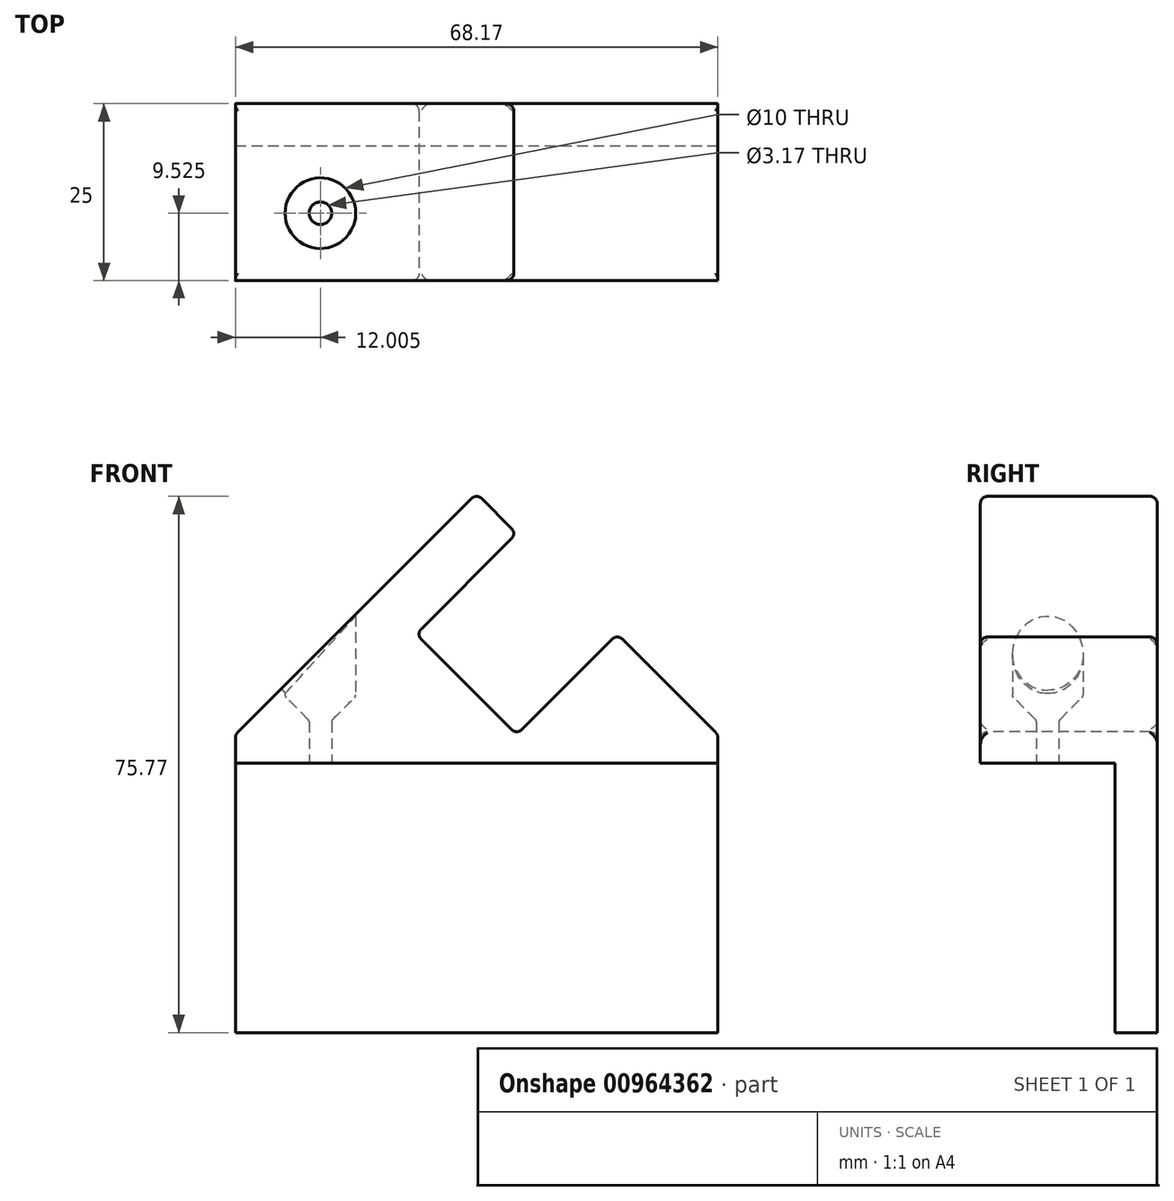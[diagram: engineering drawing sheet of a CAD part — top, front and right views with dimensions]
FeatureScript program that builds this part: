
annotation { "Feature Type Name" : "Feature", "Feature Type Description" : "" }
export const myFeature = defineFeature(function(context is Context, id is Id, definition is map)
    precondition{}
    {
        {
            var Q0;
            Q0=qCreatedBy(makeId("Front.planeOp"),FACE);
            var sketch = newSketch(context, id + "F0", { "sketchPlane" : qUnion([Q0])});
            skLineSegment(sketch, "E0", {"start": v(-68.17, 42.1) * mm, "end": v(-68.17, 0) * mm});
            skLineSegment(sketch, "E1", {"start": v(-68.17, 0) * mm, "end": v(0, 0) * mm});
            skLineSegment(sketch, "E2", {"start": v(0, 0) * mm, "end": v(0, 42.1) * mm});
            skLineSegment(sketch, "E3", {"start": v(0, 42.1) * mm, "end": v(-14.21, 56.31) * mm});
            skLineSegment(sketch, "E4", {"start": v(-14.21, 56.31) * mm, "end": v(-28.43, 42.1) * mm});
            skLineSegment(sketch, "E5", {"start": v(-28.43, 42.1) * mm, "end": v(-42.64, 56.31) * mm});
            skLineSegment(sketch, "E6", {"start": v(-42.64, 56.31) * mm, "end": v(-28.43, 70.53) * mm});
            skLineSegment(sketch, "E7", {"start": v(-28.43, 70.53) * mm, "end": v(-34.08, 76.18) * mm});
            skLineSegment(sketch, "E8", {"start": v(-34.08, 76.18) * mm, "end": v(-68.17, 42.1) * mm});
            skLineSegment(sketch, "E9", {"start": v(0, 42.1) * mm, "end": v(-68.17, 42.1) * mm, "construction": true});
            skLineSegment(sketch, "E10", {"start": v(-68.17, 38.1) * mm, "end": v(0, 38.1) * mm, "construction": true});
            skLineSegment(sketch, "E11", {"start": v(-28.43, 70.53) * mm, "end": v(-14.21, 56.31) * mm, "construction": true});
            skSolve(sketch);
        }
        {
            var Q0;
            Q0=makeQuery(id+"F0.imprint","IMPRINT",FACE,{"disambiguationData":[TD([[makeQuery(id+"F0.imprint","IMPRINT",EDGE,{"derivedFrom":sQuery(id+"F0.wireOp",EDGE,"E0")}),1.0]])]});
            extrude(context, id + "F1", {"entities" : qUnion([Q0]), "depth" : 25 * mm, "offsetDistance" : 25 * mm});
        }
        {
            var Q0;
            Q0=makeQuery(id+"F1.opExtrude","SWEPT_FACE",FACE,{"disambiguationData":[OSD([sQuery(id+"F0.wireOp",EDGE,"E2")])]});
            var sketch = newSketch(context, id + "F2", { "sketchPlane" : qUnion([Q0])});
            skLineSegment(sketch, "E12.0.0", {"start": v(0, 0) * mm, "end": v(0, 42.1) * mm, "construction": true});
            skLineSegment(sketch, "E12.0.1", {"start": v(0, 42.1) * mm, "end": v(-25, 42.1) * mm, "construction": true});
            skLineSegment(sketch, "E12.0.2", {"start": v(-25, 42.1) * mm, "end": v(-25, 0) * mm, "construction": true});
            skLineSegment(sketch, "E12.0.3", {"start": v(-25, 0) * mm, "end": v(0, 0) * mm, "construction": true});
            skLineSegment(sketch, "E13.bottom", {"start": v(-25, 38.1) * mm, "end": v(-5.95, 38.1) * mm});
            skLineSegment(sketch, "E13.top", {"start": v(-25, 0) * mm, "end": v(-5.95, 0) * mm});
            skLineSegment(sketch, "E13.left", {"start": v(-25, 38.1) * mm, "end": v(-25, 0) * mm});
            skLineSegment(sketch, "E13.right", {"start": v(-5.95, 38.1) * mm, "end": v(-5.95, 0) * mm});
            skSolve(sketch);
        }
        {
            var Q0;
            Q0=makeQuery(id+"F2.imprint","IMPRINT",FACE,{"disambiguationData":[TD([[makeQuery(id+"F2.imprint","IMPRINT",EDGE,{"derivedFrom":sQuery(id+"F2.wireOp",EDGE,"E13.bottom")}),-1.0]])]});
            extrude(context, id + "F3", {"entities" : qUnion([Q0]), "operationType" : NewBodyOperationType.REMOVE, "endBound" : BoundingType.THROUGH_ALL, "oppositeDirection" : true, "depth" : 25 * mm, "offsetDistance" : 25 * mm});
        }
        {
            var Q0;
            Q0=makeQuery(id+"F1.opExtrude","SWEPT_FACE",FACE,{"disambiguationData":[OSD([sQuery(id+"F0.wireOp",EDGE,"E6")])]});
            var Q1;
            Q1=makeQuery(id+"F1.opExtrude","SWEPT_FACE",FACE,{"disambiguationData":[OSD([sQuery(id+"F0.wireOp",EDGE,"E4")])]});
            var Q2;
            Q2=makeQuery(id+"F1.opExtrude","SWEPT_FACE",FACE,{"disambiguationData":[OSD([sQuery(id+"F0.wireOp",EDGE,"E8")])]});
            var Q3;
            Q3=makeQuery(id+"F1.opExtrude","SWEPT_FACE",FACE,{"disambiguationData":[OSD([sQuery(id+"F0.wireOp",EDGE,"E3")])]});
            var Q4;
            Q4=makeQuery(id+"F1.opExtrude","SWEPT_FACE",FACE,{"disambiguationData":[OSD([sQuery(id+"F0.wireOp",EDGE,"E7")])]});
            fillet(context, id + "F4", {"entities" : qUnion([Q0, Q1, Q2, Q3, Q4]), "radius" : 1 * mm, "tangentPropagation" : true, "allowEdgeOverflow" : false});
        }
        {
            var Q0;
            Q0=makeQuery(id+"F3.boolean.opBoolean","COPY",FACE,{"derivedFrom":makeQuery(id+"F3.opExtrude","SWEPT_FACE",FACE,{"disambiguationData":[OSD([sQuery(id+"F2.wireOp",EDGE,"E13.bottom")])]})});
            var sketch = newSketch(context, id + "F5", { "sketchPlane" : qUnion([Q0])});
            skLineSegment(sketch, "E14.0.0", {"start": v(-68.17, 25) * mm, "end": v(-68.17, 5.95) * mm, "construction": true});
            skLineSegment(sketch, "E14.0.1", {"start": v(-68.17, 5.95) * mm, "end": v(0, 5.95) * mm, "construction": true});
            skLineSegment(sketch, "E14.0.2", {"start": v(0, 5.95) * mm, "end": v(0, 25) * mm, "construction": true});
            skLineSegment(sketch, "E14.0.3", {"start": v(0, 25) * mm, "end": v(-68.17, 25) * mm, "construction": true});
            skLineSegment(sketch, "E15", {"start": v(-68.17, 15.48) * mm, "end": v(0, 15.48) * mm, "construction": true});
            skLineSegment(sketch, "E16", {"start": v(-56.17, 25) * mm, "end": v(-56.17, 5.95) * mm, "construction": true});
            skCircle(sketch, "E17", {"center": v(-56.17, 15.48) * mm, "radius": 1.59 * mm});
            skCircle(sketch, "E18", {"center": v(-56.17, 15.48) * mm, "radius": 5 * mm});
            skSolve(sketch);
        }
        {
            var Q0;
            Q0=makeQuery(id+"F5.imprint","IMPRINT",FACE,{"disambiguationData":[TD([[makeQuery(id+"F5.imprint","IMPRINT",EDGE,{"derivedFrom":sQuery(id+"F5.wireOp",EDGE,"E17")}),1.0]])]});
            var Q1;
            Q1=makeQuery(id+"F5.imprint","IMPRINT",FACE,{"disambiguationData":[TD([[makeQuery(id+"F5.imprint","IMPRINT",EDGE,{"derivedFrom":sQuery(id+"F5.wireOp",EDGE,"E17")}),-1.0]])]});
            extrude(context, id + "F6", {"entities" : qUnion([Q0, Q1]), "operationType" : NewBodyOperationType.REMOVE, "endBound" : BoundingType.THROUGH_ALL, "oppositeDirection" : true, "depth" : 25 * mm, "offsetDistance" : 25 * mm});
        }
        {
            var Q0;
            Q0=makeQuery(id+"F5.imprint","IMPRINT",FACE,{"disambiguationData":[TD([[makeQuery(id+"F5.imprint","IMPRINT",EDGE,{"derivedFrom":sQuery(id+"F5.wireOp",EDGE,"E17")}),-1.0]])]});
            extrude(context, id + "F7", {"entities" : qUnion([Q0]), "operationType" : NewBodyOperationType.ADD, "oppositeDirection" : true, "depth" : 10 * mm, "offsetDistance" : 25 * mm});
        }
        {
            var Q0;
            Q0=makeQuery(id+"F7.opExtrude","CAP_EDGE",EDGE,{"disambiguationData":[OSD([sQuery(id+"F5.wireOp",EDGE,"E17")])],"isStart":false});
            chamfer(context, id + "F8", {"entities" : qUnion([Q0]), "width" : 4 * mm, "tangentPropagation" : true});
        }
        {
            var Q0;
            Q0=makeQuery(id+"F6.boolean.opBoolean","COPY",FACE,{"derivedFrom":makeQuery(id+"F6.opExtrude","SWEPT_FACE",FACE,{"disambiguationData":[OSD([sQuery(id+"F5.wireOp",EDGE,"E18")])]})});
            var Q1;
            {var subQ0=sQuery(id+"F5.wireOp",EDGE,"E17");Q1=makeQuery(id+"F8.opChamfer","BLEND_EDGE",EDGE,{"blendedFrom":[makeQuery(id+"F7.opExtrude","CAP_EDGE",EDGE,{"disambiguationData":[OSD([subQ0])],"isStart":false}),makeQuery(id+"F7.opExtrude","SWEPT_FACE",FACE,{"disambiguationData":[OSD([subQ0])]})],"blendedInto":[makeQuery(id+"F7.opExtrude","SWEPT_FACE",FACE,{"disambiguationData":[OSD([subQ0])]})]});}
            fillet(context, id + "F9", {"entities" : qUnion([Q0, Q1]), "radius" : .5 * mm, "tangentPropagation" : true, "allowEdgeOverflow" : false});
        }
    });
